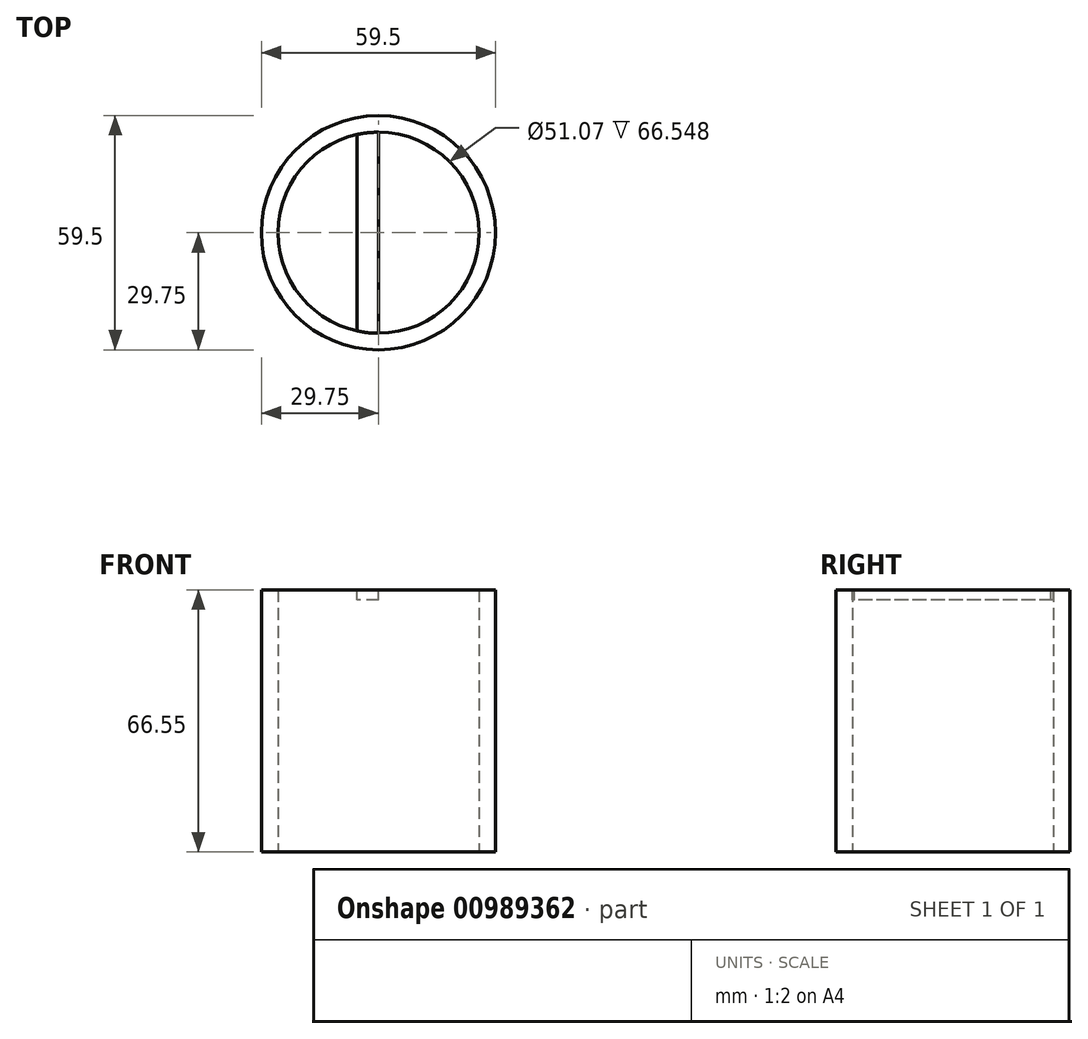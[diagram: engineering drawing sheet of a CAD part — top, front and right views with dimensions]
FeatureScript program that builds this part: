
annotation { "Feature Type Name" : "Feature", "Feature Type Description" : "" }
export const myFeature = defineFeature(function(context is Context, id is Id, definition is map)
    precondition{}
    {
        {
            var Q0;
            Q0=qCreatedBy(makeId("Top.planeOp"),FACE);
            var sketch = newSketch(context, id + "F0", { "sketchPlane" : qUnion([Q0])});
            skCircle(sketch, "E0", {"center": v(0, 0) * mm, "radius": 29.75 * mm});
            skCircle(sketch, "E1", {"center": v(0, 0) * mm, "radius": 25.53 * mm});
            skSolve(sketch);
        }
        {
            var Q0;
            Q0=makeQuery(id+"F0.imprint","IMPRINT",FACE,{"disambiguationData":[TD([[makeQuery(id+"F0.imprint","IMPRINT",EDGE,{"derivedFrom":sQuery(id+"F0.wireOp",EDGE,"E0")}),1.0]])]});
            extrude(context, id + "F1", {"entities" : qUnion([Q0]), "depth" : 66.55 * mm, "offsetDistance" : 25.4 * mm});
        }
        {
            var Q0;
            Q0=makeQuery(id+"F1.opExtrude","CAP_FACE",FACE,{"disambiguationData":[OSD([sQuery(id+"F0.wireOp",EDGE,"E0"),sQuery(id+"F0.wireOp",EDGE,"E1")])],"isStart":false});
            var sketch = newSketch(context, id + "F2", { "sketchPlane" : qUnion([Q0])});
            skLineSegment(sketch, "E2.bottom", {"start": v(0, 29.75) * mm, "end": v(-5.4, 29.75) * mm});
            skLineSegment(sketch, "E2.top", {"start": v(0, -29.25) * mm, "end": v(-5.4, -29.25) * mm});
            skLineSegment(sketch, "E2.left", {"start": v(0, 29.75) * mm, "end": v(0, -29.25) * mm});
            skLineSegment(sketch, "E2.right", {"start": v(-5.4, 29.75) * mm, "end": v(-5.4, -29.25) * mm});
            skSolve(sketch);
        }
        {
            var Q0;
            {var subQ0=sQuery(id+"F2.wireOp",EDGE,"E2.left");var subQ1=makeQuery(id+"F1.opExtrude","CAP_EDGE",EDGE,{"disambiguationData":[OSD([sQuery(id+"F0.wireOp",EDGE,"E1")])],"isStart":false});var subQ2=makeQuery(id+"F2.imprint","INTERSECT",VERTEX,{"disambiguationData":[OD(0.0)],"derivedFrom":[subQ1,subQ0]});Q0=makeQuery(id+"F2.imprint","IMPRINT",FACE,{"disambiguationData":[TD([[makeQuery(id+"F2.imprint","IMPRINT",EDGE,{"disambiguationData":[TD([[subQ2,-1.0]])],"derivedFrom":subQ0}),-1.0]])]});}
            extrude(context, id + "F3", {"entities" : qUnion([Q0]), "oppositeDirection" : true, "depth" : 2.54 * mm, "offsetDistance" : 25.4 * mm});
        }
    });
